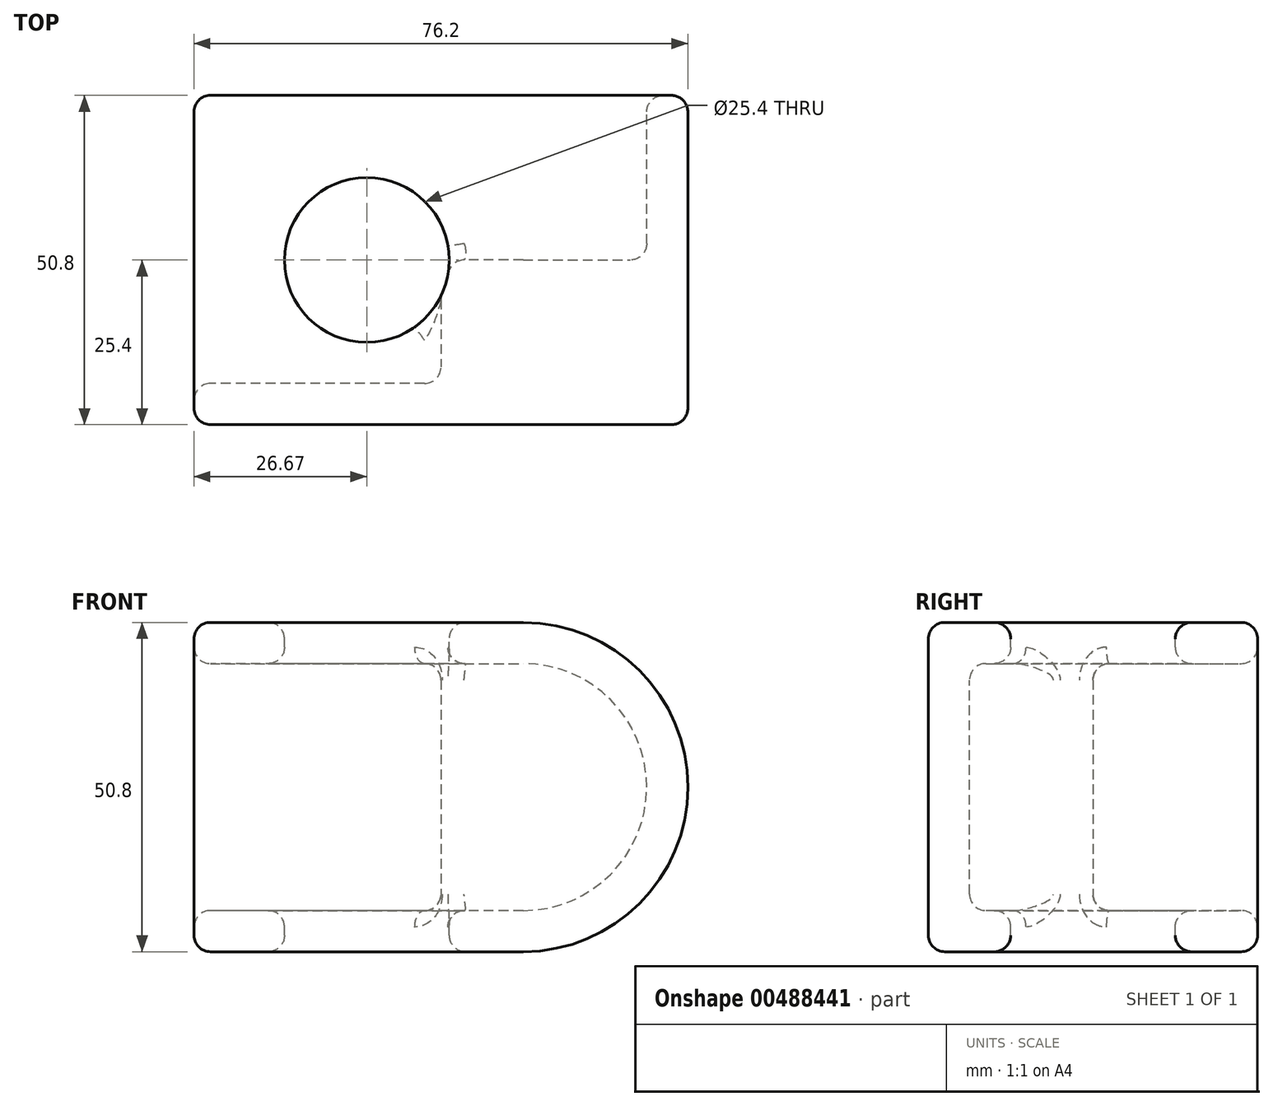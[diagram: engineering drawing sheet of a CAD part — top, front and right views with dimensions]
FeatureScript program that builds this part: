
annotation { "Feature Type Name" : "Feature", "Feature Type Description" : "" }
export const myFeature = defineFeature(function(context is Context, id is Id, definition is map)
    precondition{}
    {
        {
            var Q0;
            Q0=qCreatedBy(makeId("Front.planeOp"),FACE);
            var sketch = newSketch(context, id + "F0", { "sketchPlane" : qUnion([Q0])});
            skLineSegment(sketch, "E0.bottom", {"start": v(0, 0) * mm, "end": v(50.8, 0) * mm});
            skLineSegment(sketch, "E0.top", {"start": v(0, 50.8) * mm, "end": v(50.8, 50.8) * mm});
            skLineSegment(sketch, "E0.left", {"start": v(0, 0) * mm, "end": v(0, 50.8) * mm});
            skLineSegment(sketch, "E0.right", {"start": v(50.8, 0) * mm, "end": v(50.8, 50.8) * mm});
            skSolve(sketch);
        }
        {
            var Q0;
            Q0=makeQuery(id+"F0.imprint","IMPRINT",FACE,{"disambiguationData":[TD([[makeQuery(id+"F0.imprint","IMPRINT",EDGE,{"derivedFrom":sQuery(id+"F0.wireOp",EDGE,"E0.bottom")}),1.0]])]});
            extrude(context, id + "F1", {"entities" : qUnion([Q0]), "depth" : 25.4 * mm});
        }
        {
            var Q0;
            Q0=makeQuery(id+"F1.opExtrude","CAP_FACE",FACE,{"disambiguationData":[OSD([sQuery(id+"F0.wireOp",EDGE,"E0.bottom"),sQuery(id+"F0.wireOp",EDGE,"E0.top"),sQuery(id+"F0.wireOp",EDGE,"E0.left"),sQuery(id+"F0.wireOp",EDGE,"E0.right")])],"isStart":false});
            var sketch = newSketch(context, id + "F2", { "sketchPlane" : qUnion([Q0])});
            skCircle(sketch, "E1", {"center": v(50.8, 25.4) * mm, "radius": 25.4 * mm});
            skSolve(sketch);
        }
        {
            var Q0;
            Q0=makeQuery(id+"F1.opExtrude","CAP_FACE",FACE,{"disambiguationData":[OSD([sQuery(id+"F0.wireOp",EDGE,"E0.bottom"),sQuery(id+"F0.wireOp",EDGE,"E0.top"),sQuery(id+"F0.wireOp",EDGE,"E0.left"),sQuery(id+"F0.wireOp",EDGE,"E0.right")])],"isStart":false});
            extrude(context, id + "F3", {"entities" : qUnion([Q0]), "operationType" : NewBodyOperationType.ADD, "depth" : 25.4 * mm});
        }
        {
            var Q0;
            {var subQ1=makeQuery(id+"F1.opExtrude","CAP_EDGE",EDGE,{"disambiguationData":[OSD([sQuery(id+"F0.wireOp",EDGE,"E0.right")])],"isStart":false});Q0=makeQuery(id+"F2.imprint","IMPRINT",FACE,{"disambiguationData":[TD([[makeQuery(id+"F2.imprint","IMPRINT",EDGE,{"derivedFrom":subQ1}),-1.0]])]});}
            extrude(context, id + "F4", {"entities" : qUnion([Q0]), "operationType" : NewBodyOperationType.ADD, "endBound" : BoundingType.SYMMETRIC, "depth" : 50.8 * mm, "offsetDistance" : 25.4 * mm});
        }
        {
            var Q0;
            {var subQ0=sQuery(id+"F0.wireOp",EDGE,"E0.left");Q0=makeQuery(id+"F3.boolean.opBoolean","MERGE",FACE,{"derivedFrom":[makeQuery(id+"F1.opExtrude","SWEPT_FACE",FACE,{"disambiguationData":[OSD([subQ0])]}),makeQuery(id+"F3.opExtrude","SWEPT_FACE",FACE,{"disambiguationData":[OSD([subQ0])]})]});}
            var sketch = newSketch(context, id + "F5", { "sketchPlane" : qUnion([Q0])});
            skLineSegment(sketch, "E2.0", {"start": v(6.35, 44.45) * mm, "end": v(6.35, 6.35) * mm});
            skLineSegment(sketch, "E2.1", {"start": v(44.45, 44.45) * mm, "end": v(6.35, 44.45) * mm});
            skLineSegment(sketch, "E2.2", {"start": v(44.45, 6.35) * mm, "end": v(44.45, 44.45) * mm});
            skLineSegment(sketch, "E2.3", {"start": v(6.35, 6.35) * mm, "end": v(44.45, 6.35) * mm});
            skSolve(sketch);
        }
        {
            var Q0;
            Q0=makeQuery(id+"F5.imprint","IMPRINT",FACE,{"disambiguationData":[TD([[makeQuery(id+"F5.imprint","IMPRINT",EDGE,{"derivedFrom":sQuery(id+"F5.wireOp",EDGE,"E2.0")}),1.0]])]});
            extrude(context, id + "F6", {"entities" : qUnion([Q0]), "operationType" : NewBodyOperationType.REMOVE, "oppositeDirection" : true, "depth" : 38.1 * mm, "offsetDistance" : 25.4 * mm});
        }
        {
            var Q0;
            {var subQ0=sQuery(id+"F0.wireOp",EDGE,"E0.right");Q0=makeQuery(id+"F4.boolean.opBoolean","MERGE",FACE,{"derivedFrom":[makeQuery(id+"F1.opExtrude","CAP_FACE",FACE,{"disambiguationData":[OSD([sQuery(id+"F0.wireOp",EDGE,"E0.bottom"),sQuery(id+"F0.wireOp",EDGE,"E0.top"),sQuery(id+"F0.wireOp",EDGE,"E0.left"),subQ0])],"isStart":true}),makeQuery(id+"F4.opExtrude","CAP_FACE",FACE,{"disambiguationData":[OSD([subQ0,sQuery(id+"F2.wireOp",EDGE,"E1")])],"isStart":true})]});}
            var sketch = newSketch(context, id + "F7", { "sketchPlane" : qUnion([Q0])});
            skLineSegment(sketch, "E3.0", {"start": v(-6.35, 44.45) * mm, "end": v(-50.8, 44.45) * mm});
            skLineSegment(sketch, "E3.1", {"start": v(-6.35, 6.35) * mm, "end": v(-6.35, 44.45) * mm});
            skLineSegment(sketch, "E3.2", {"start": v(-50.8, 6.35) * mm, "end": v(-6.35, 6.35) * mm});
            skArc(sketch, "E3.3", {"start": v(-50.8, 44.45) * mm, "mid": v(-69.85, 25.4) * mm, "end": v(-50.8, 6.35) * mm});
            skSolve(sketch);
        }
        {
            var Q0;
            Q0=makeQuery(id+"F7.imprint","IMPRINT",FACE,{"disambiguationData":[TD([[makeQuery(id+"F7.imprint","IMPRINT",EDGE,{"derivedFrom":sQuery(id+"F7.wireOp",EDGE,"E3.0")}),1.0]])]});
            extrude(context, id + "F8", {"entities" : qUnion([Q0]), "operationType" : NewBodyOperationType.REMOVE, "oppositeDirection" : true, "depth" : 25.4 * mm, "offsetDistance" : 25.4 * mm});
        }
        {
            var Q0;
            Q0=makeQuery(id+"F6.boolean.opBoolean","COPY",FACE,{"derivedFrom":makeQuery(id+"F6.opExtrude","SWEPT_FACE",FACE,{"disambiguationData":[OSD([sQuery(id+"F5.wireOp",EDGE,"E2.0")])]})});
            extrude(context, id + "F9", {"entities" : qUnion([Q0]), "operationType" : NewBodyOperationType.REMOVE, "oppositeDirection" : true, "depth" : 25.4 * mm, "offsetDistance" : 25.4 * mm});
        }
        {
            var Q0;
            Q0=makeQuery(id+"F3.opExtrude","CAP_EDGE",EDGE,{"disambiguationData":[OSD([sQuery(id+"F0.wireOp",EDGE,"E0.left")])],"isStart":false});
            var Q1;
            {var subQ0=sQuery(id+"F0.wireOp",EDGE,"E0.right");Q1=makeQuery(id+"F4.boolean.opBoolean","MERGE",FACE,{"derivedFrom":[makeQuery(id+"F3.opExtrude","CAP_FACE",FACE,{"disambiguationData":[OSD([sQuery(id+"F0.wireOp",EDGE,"E0.bottom"),sQuery(id+"F0.wireOp",EDGE,"E0.top"),sQuery(id+"F0.wireOp",EDGE,"E0.left"),subQ0])],"isStart":false}),makeQuery(id+"F4.opExtrude","CAP_FACE",FACE,{"disambiguationData":[OSD([subQ0,sQuery(id+"F2.wireOp",EDGE,"E1")])],"isStart":false})]});}
            var Q2;
            {var subQ0=sQuery(id+"F0.wireOp",EDGE,"E0.bottom");Q2=makeQuery(id+"F3.boolean.opBoolean","MERGE",FACE,{"derivedFrom":[makeQuery(id+"F1.opExtrude","SWEPT_FACE",FACE,{"disambiguationData":[OSD([subQ0])]}),makeQuery(id+"F3.opExtrude","SWEPT_FACE",FACE,{"disambiguationData":[OSD([subQ0])]})]});}
            var Q3;
            {var subQ0=sQuery(id+"F0.wireOp",EDGE,"E0.top");Q3=makeQuery(id+"F3.boolean.opBoolean","MERGE",FACE,{"derivedFrom":[makeQuery(id+"F1.opExtrude","SWEPT_FACE",FACE,{"disambiguationData":[OSD([subQ0])]}),makeQuery(id+"F3.opExtrude","SWEPT_FACE",FACE,{"disambiguationData":[OSD([subQ0])]})]});}
            var Q4;
            {var subQ0=sQuery(id+"F0.wireOp",EDGE,"E0.right");Q4=makeQuery(id+"F4.boolean.opBoolean","MERGE",FACE,{"derivedFrom":[makeQuery(id+"F1.opExtrude","CAP_FACE",FACE,{"disambiguationData":[OSD([sQuery(id+"F0.wireOp",EDGE,"E0.bottom"),sQuery(id+"F0.wireOp",EDGE,"E0.top"),sQuery(id+"F0.wireOp",EDGE,"E0.left"),subQ0])],"isStart":true}),makeQuery(id+"F4.opExtrude","CAP_FACE",FACE,{"disambiguationData":[OSD([subQ0,sQuery(id+"F2.wireOp",EDGE,"E1")])],"isStart":true})]});}
            var Q5;
            {var subQ0=sQuery(id+"F0.wireOp",EDGE,"E0.left");Q5=makeQuery(id+"F3.boolean.opBoolean","MERGE",FACE,{"derivedFrom":[makeQuery(id+"F1.opExtrude","SWEPT_FACE",FACE,{"disambiguationData":[OSD([subQ0])]}),makeQuery(id+"F3.opExtrude","SWEPT_FACE",FACE,{"disambiguationData":[OSD([subQ0])]})]});}
            var Q6;
            Q6=makeQuery(id+"F8.boolean.opBoolean","COPY",EDGE,{"derivedFrom":makeQuery(id+"F8.opExtrude","CAP_EDGE",EDGE,{"disambiguationData":[OSD([sQuery(id+"F7.wireOp",EDGE,"E3.3")])],"isStart":false})});
            var Q7;
            Q7=makeQuery(id+"F6.boolean.opBoolean","COPY",EDGE,{"derivedFrom":makeQuery(id+"F6.opExtrude","SWEPT_EDGE",EDGE,{"disambiguationData":[OSD([sQuery(id+"F5.wireOp",EDGE,"E2.1"),sQuery(id+"F5.wireOp",EDGE,"E2.2")])]})});
            var Q8;
            Q8=makeQuery(id+"F6.boolean.opBoolean","COPY",EDGE,{"derivedFrom":makeQuery(id+"F6.opExtrude","SWEPT_EDGE",EDGE,{"disambiguationData":[OSD([sQuery(id+"F5.wireOp",EDGE,"E2.2"),sQuery(id+"F5.wireOp",EDGE,"E2.3")])]})});
            var Q9;
            Q9=makeQuery(id+"F6.boolean.opBoolean","COPY",EDGE,{"derivedFrom":makeQuery(id+"F6.opExtrude","CAP_EDGE",EDGE,{"disambiguationData":[OSD([sQuery(id+"F5.wireOp",EDGE,"E2.2")])],"isStart":false})});
            fillet(context, id + "F10", {"entities" : qUnion([Q0, Q1, Q2, Q3, Q4, Q5, Q6, Q7, Q8, Q9]), "radius" : 2.54 * mm, "tangentPropagation" : true, "allowEdgeOverflow" : false});
        }
        {
            var Q0;
            {var subQ0=sQuery(id+"F0.wireOp",EDGE,"E0.top");Q0=makeQuery(id+"F3.boolean.opBoolean","MERGE",FACE,{"derivedFrom":[makeQuery(id+"F1.opExtrude","SWEPT_FACE",FACE,{"disambiguationData":[OSD([subQ0])]}),makeQuery(id+"F3.opExtrude","SWEPT_FACE",FACE,{"disambiguationData":[OSD([subQ0])]})]});}
            var sketch = newSketch(context, id + "F11", { "sketchPlane" : qUnion([Q0])});
            skCircle(sketch, "E4", {"center": v(26.67, -25.4) * mm, "radius": 12.7 * mm});
            skPoint(sketch, "E4.centerSnap0", {"position": v(2.54, -25.4) * mm});
            skPoint(sketch, "E4.centerSnap1", {"position": v(26.67, -2.54) * mm});
            skSolve(sketch);
        }
        {
            var Q0;
            Q0 = qSketchRegion(id + "F11", true);
            extrude(context, id + "F12", {"entities" : qUnion([Q0]), "operationType" : NewBodyOperationType.REMOVE, "oppositeDirection" : true, "depth" : 63.75 * mm, "offsetDistance" : 25.4 * mm});
        }
        {
            var Q0;
            Q0=makeQuery(id+"F12.boolean.opBoolean","COPY",FACE,{"derivedFrom":makeQuery(id+"F12.opExtrude","SWEPT_FACE",FACE,{"disambiguationData":[OSD([sQuery(id+"F11.wireOp",EDGE,"E4")])]})});
            var Q1;
            Q1=makeQuery(id+"F6.boolean.opBoolean","COPY",EDGE,{"derivedFrom":makeQuery(id+"F6.opExtrude","CAP_EDGE",EDGE,{"disambiguationData":[OSD([sQuery(id+"F5.wireOp",EDGE,"E2.1")])],"isStart":false})});
            var Q2;
            Q2=makeQuery(id+"F6.boolean.opBoolean","COPY",EDGE,{"derivedFrom":makeQuery(id+"F6.opExtrude","CAP_EDGE",EDGE,{"disambiguationData":[OSD([sQuery(id+"F5.wireOp",EDGE,"E2.3")])],"isStart":false})});
            fillet(context, id + "F13", {"entities" : qUnion([Q0, Q1, Q2]), "radius" : 2.54 * mm, "tangentPropagation" : true, "allowEdgeOverflow" : false});
        }
    });
